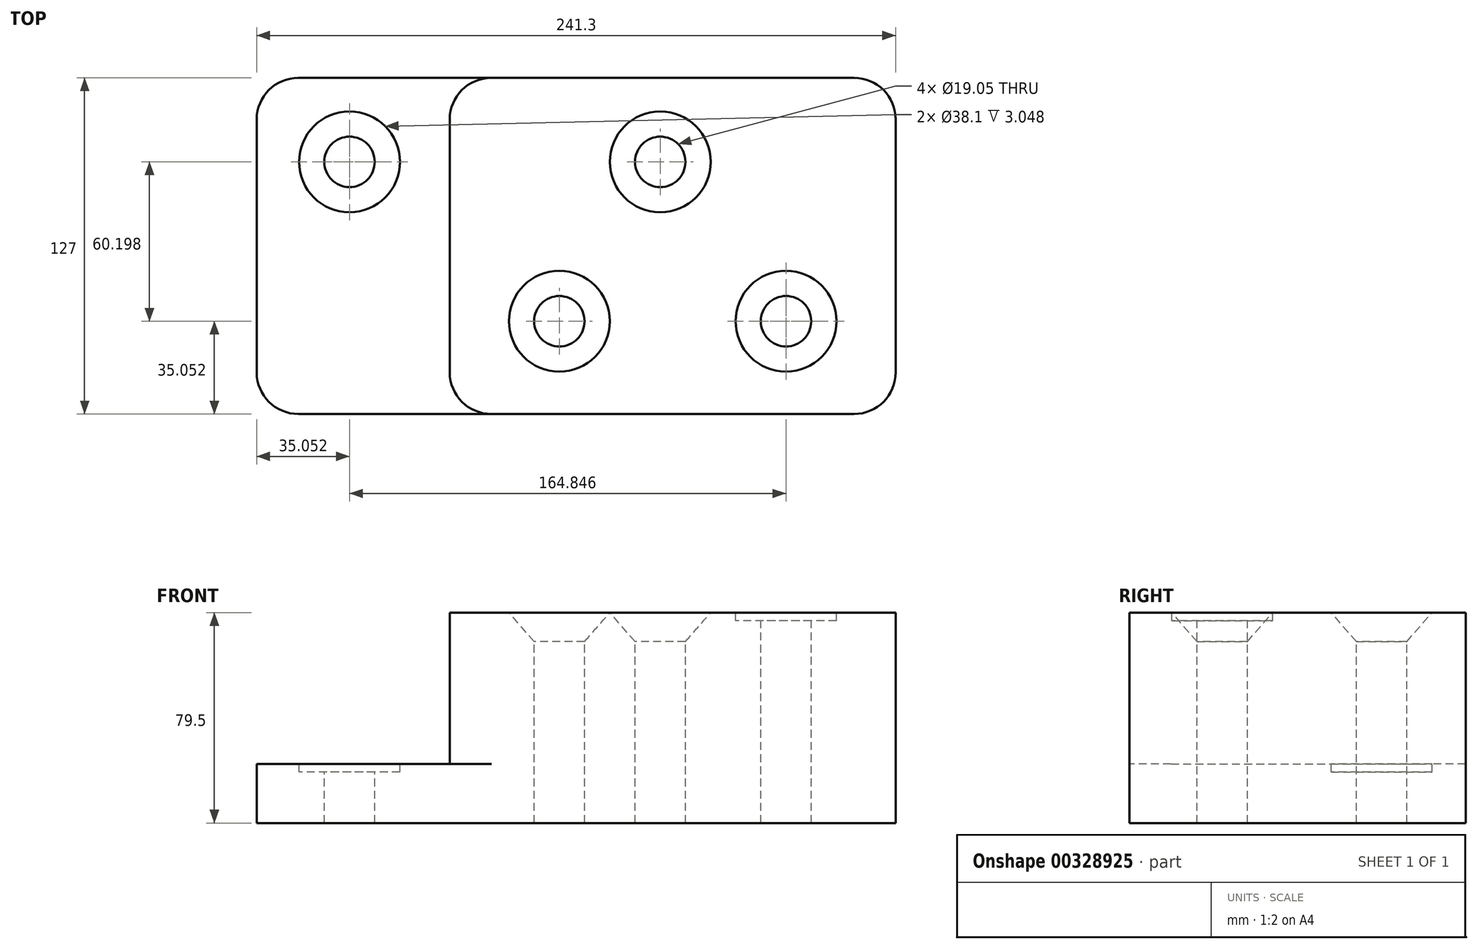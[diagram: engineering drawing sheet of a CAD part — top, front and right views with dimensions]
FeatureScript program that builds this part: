
annotation { "Feature Type Name" : "Feature", "Feature Type Description" : "" }
export const myFeature = defineFeature(function(context is Context, id is Id, definition is map)
    precondition{}
    {
        {
            var Q0;
            Q0=qCreatedBy(makeId("Front.planeOp"),FACE);
            var sketch = newSketch(context, id + "F0", { "sketchPlane" : qUnion([Q0])});
            skLineSegment(sketch, "E0", {"start": v(0, 0) * mm, "end": v(241.3, 0) * mm});
            skLineSegment(sketch, "E1", {"start": v(241.3, 0) * mm, "end": v(241.3, 79.5) * mm});
            skLineSegment(sketch, "E2", {"start": v(241.3, 79.5) * mm, "end": v(72.9, 79.5) * mm});
            skLineSegment(sketch, "E3", {"start": v(0, 0) * mm, "end": v(0, 22.35) * mm});
            skLineSegment(sketch, "E4", {"start": v(0, 22.35) * mm, "end": v(72.9, 22.35) * mm});
            skLineSegment(sketch, "E5", {"start": v(72.9, 22.35) * mm, "end": v(72.9, 79.5) * mm});
            skSolve(sketch);
        }
        {
            var Q0;
            Q0=makeQuery(id+"F0.imprint","IMPRINT",FACE,{"disambiguationData":[TD([[makeQuery(id+"F0.imprint","IMPRINT",EDGE,{"derivedFrom":sQuery(id+"F0.wireOp",EDGE,"E0")}),1.0]])]});
            extrude(context, id + "F1", {"entities" : qUnion([Q0]), "depth" : 127 * mm});
        }
        {
            var Q0;
            Q0=makeQuery(id+"F1.opExtrude","CAP_EDGE",EDGE,{"disambiguationData":[OSD([sQuery(id+"F0.wireOp",EDGE,"E3")])],"isStart":false});
            var Q1;
            Q1=makeQuery(id+"F1.opExtrude","CAP_EDGE",EDGE,{"disambiguationData":[OSD([sQuery(id+"F0.wireOp",EDGE,"E5")])],"isStart":false});
            var Q2;
            Q2=makeQuery(id+"F1.opExtrude","CAP_EDGE",EDGE,{"disambiguationData":[OSD([sQuery(id+"F0.wireOp",EDGE,"E1")])],"isStart":false});
            var Q3;
            Q3=makeQuery(id+"F1.opExtrude","CAP_EDGE",EDGE,{"disambiguationData":[OSD([sQuery(id+"F0.wireOp",EDGE,"E1")])],"isStart":true});
            var Q4;
            Q4=makeQuery(id+"F1.opExtrude","CAP_EDGE",EDGE,{"disambiguationData":[OSD([sQuery(id+"F0.wireOp",EDGE,"E5")])],"isStart":true});
            var Q5;
            Q5=makeQuery(id+"F1.opExtrude","CAP_EDGE",EDGE,{"disambiguationData":[OSD([sQuery(id+"F0.wireOp",EDGE,"E3")])],"isStart":true});
            fillet(context, id + "F2", {"entities" : qUnion([Q0, Q1, Q2, Q3, Q4, Q5]), "radius" : 15.75 * mm, "tangentPropagation" : true, "allowEdgeOverflow" : false});
        }
        {
            var Q0;
            Q0=makeQuery(id+"F1.opExtrude","SWEPT_FACE",FACE,{"disambiguationData":[OSD([sQuery(id+"F0.wireOp",EDGE,"E4")])]});
            var sketch = newSketch(context, id + "F3", { "sketchPlane" : qUnion([Q0])});
            skCircle(sketch, "E6", {"center": v(35.05, -31.75) * mm, "radius": 19.05 * mm});
            skCircle(sketch, "E7", {"center": v(35.05, -31.75) * mm, "radius": 9.53 * mm});
            skSolve(sketch);
        }
        {
            var Q0;
            Q0=makeQuery(id+"F3.imprint","IMPRINT",FACE,{"disambiguationData":[TD([[makeQuery(id+"F3.imprint","IMPRINT",EDGE,{"derivedFrom":sQuery(id+"F3.wireOp",EDGE,"E6")}),1.0]])]});
            extrude(context, id + "F4", {"entities" : qUnion([Q0]), "operationType" : NewBodyOperationType.REMOVE, "oppositeDirection" : true, "depth" : 3.05 * mm});
        }
        {
            var Q0;
            Q0=makeQuery(id+"F4.boolean.opBoolean","SPLIT",FACE,{"disambiguationData":[TD([makeQuery(id+"F4.opExtrude","SWEPT_FACE",FACE,{"disambiguationData":[OSD([sQuery(id+"F3.wireOp",EDGE,"E7")])]})])],"derivedFrom":makeQuery(id+"F1.opExtrude","SWEPT_FACE",FACE,{"disambiguationData":[OSD([sQuery(id+"F0.wireOp",EDGE,"E4")])]})});
            extrude(context, id + "F5", {"entities" : qUnion([Q0]), "operationType" : NewBodyOperationType.REMOVE, "endBound" : BoundingType.THROUGH_ALL, "oppositeDirection" : true, "depth" : 25.4 * mm});
        }
        {
            var Q0;
            Q0=makeQuery(id+"F1.opExtrude","SWEPT_FACE",FACE,{"disambiguationData":[OSD([sQuery(id+"F0.wireOp",EDGE,"E2")])]});
            var sketch = newSketch(context, id + "F6", { "sketchPlane" : qUnion([Q0])});
            skCircle(sketch, "E8", {"center": v(199.9, -91.95) * mm, "radius": 19.05 * mm});
            skCircle(sketch, "E9", {"center": v(199.9, -91.95) * mm, "radius": 9.53 * mm});
            skCircle(sketch, "E10", {"center": v(114.3, -91.95) * mm, "radius": 19.05 * mm});
            skCircle(sketch, "E11", {"center": v(114.3, -91.95) * mm, "radius": 9.53 * mm});
            skCircle(sketch, "E12", {"center": v(152.4, -31.75) * mm, "radius": 19.05 * mm});
            skCircle(sketch, "E13", {"center": v(152.4, -31.75) * mm, "radius": 9.53 * mm});
            skSolve(sketch);
        }
        {
            var Q0;
            Q0=makeQuery(id+"F6.imprint","IMPRINT",FACE,{"disambiguationData":[TD([[makeQuery(id+"F6.imprint","IMPRINT",EDGE,{"derivedFrom":sQuery(id+"F6.wireOp",EDGE,"E8")}),1.0]])]});
            var Q1;
            Q1=sQuery(id+"F6.wireOp",EDGE,"E8");
            extrude(context, id + "F7", {"entities" : qUnion([Q0]), "operationType" : NewBodyOperationType.REMOVE, "surfaceEntities" : qUnion([Q1]), "oppositeDirection" : true, "depth" : 3.05 * mm});
        }
        {
            var Q0;
            Q0=makeQuery(id+"F7.boolean.opBoolean","SPLIT",FACE,{"disambiguationData":[TD([makeQuery(id+"F7.opExtrude","SWEPT_FACE",FACE,{"disambiguationData":[OSD([sQuery(id+"F6.wireOp",EDGE,"E9")])]})])],"derivedFrom":makeQuery(id+"F1.opExtrude","SWEPT_FACE",FACE,{"disambiguationData":[OSD([sQuery(id+"F0.wireOp",EDGE,"E2")])]})});
            extrude(context, id + "F8", {"entities" : qUnion([Q0]), "operationType" : NewBodyOperationType.REMOVE, "endBound" : BoundingType.THROUGH_ALL, "oppositeDirection" : true, "depth" : 25.4 * mm});
        }
        {
            var Q0;
            Q0=makeQuery(id+"F6.imprint","IMPRINT",FACE,{"disambiguationData":[TD([[makeQuery(id+"F6.imprint","IMPRINT",EDGE,{"derivedFrom":sQuery(id+"F6.wireOp",EDGE,"E11")}),1.0]])]});
            var Q1;
            Q1=makeQuery(id+"F6.imprint","IMPRINT",FACE,{"disambiguationData":[TD([[makeQuery(id+"F6.imprint","IMPRINT",EDGE,{"derivedFrom":sQuery(id+"F6.wireOp",EDGE,"E13")}),1.0]])]});
            extrude(context, id + "F9", {"entities" : qUnion([Q0, Q1]), "operationType" : NewBodyOperationType.REMOVE, "endBound" : BoundingType.THROUGH_ALL, "oppositeDirection" : true, "depth" : 25.4 * mm});
        }
        {
            var Q0;
            Q0=sQuery(id+"F6.wireOp",VERTEX,"E10.center");
            var Q1;
            Q1=sQuery(id+"F6.wireOp",VERTEX,"E12.center");
            var Q2;
            Q2=makeQuery(id+"F1.opExtrude","SWEPT_BODY",BODY,{"disambiguationData":[OSD([sQuery(id+"F0.wireOp",EDGE,"E0"),sQuery(id+"F0.wireOp",EDGE,"E1"),sQuery(id+"F0.wireOp",EDGE,"E2"),sQuery(id+"F0.wireOp",EDGE,"E3"),sQuery(id+"F0.wireOp",EDGE,"E4"),sQuery(id+"F0.wireOp",EDGE,"E5")])]});
            hole(context, id + "F10", {"style" : HoleStyle.C_SINK, "endStyle" : HoleEndStyle.THROUGH, "holeDiameter" : 12.7 * mm, "cSinkDiameter" : 38.1 * mm, "cSinkAngle" : 82 * degree, "tappedDepth" : 12.7 * mm, "tapClearance" : 3, "locations" : qUnion([Q0, Q1]), "scope" : qUnion([Q2])});
        }
    });
